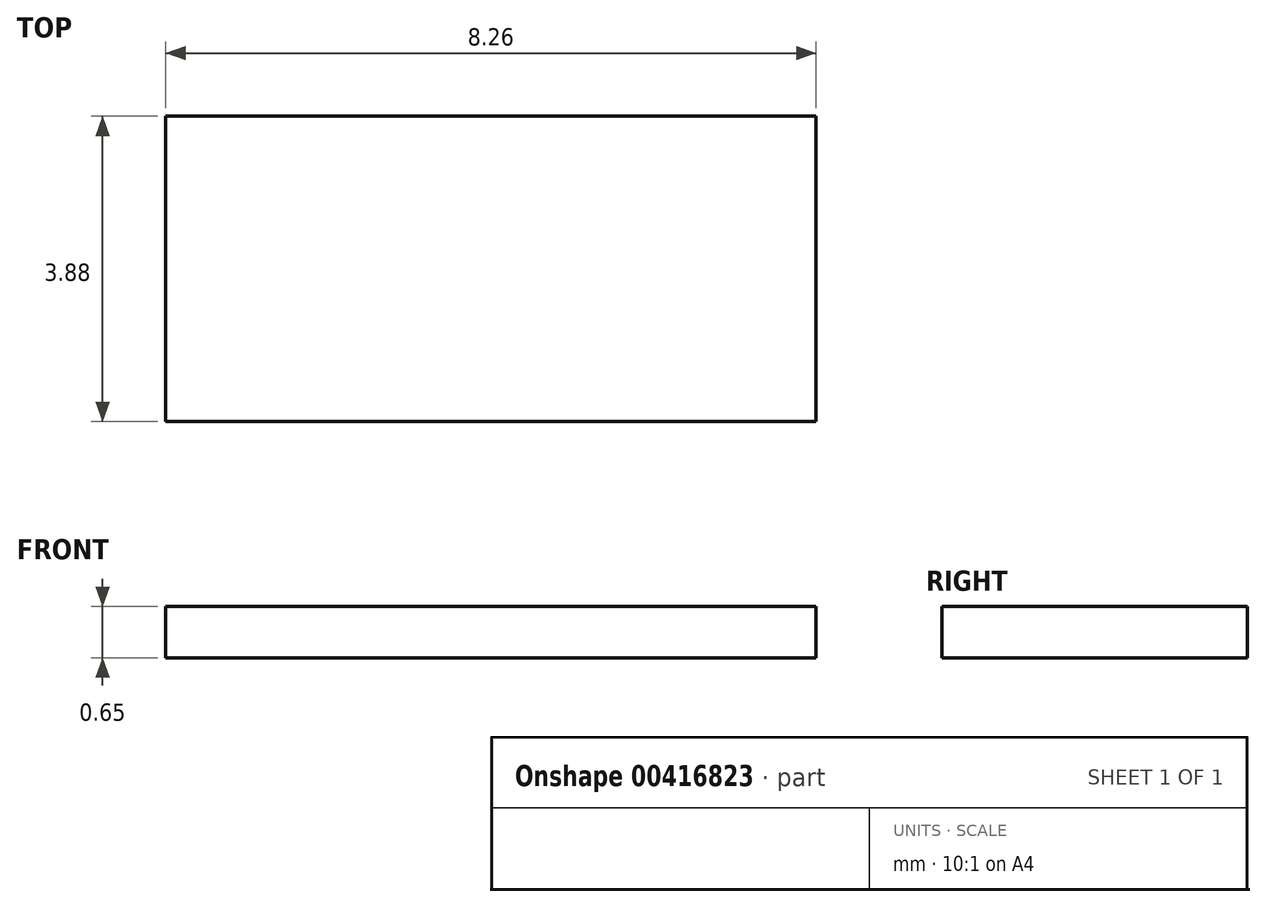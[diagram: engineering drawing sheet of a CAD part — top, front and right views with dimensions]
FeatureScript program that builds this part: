
annotation { "Feature Type Name" : "Feature", "Feature Type Description" : "" }
export const myFeature = defineFeature(function(context is Context, id is Id, definition is map)
    precondition{}
    {
        {
            var Q0;
            Q0=qCreatedBy(makeId("Top.planeOp"),FACE);
            var sketch = newSketch(context, id + "F0", { "sketchPlane" : qUnion([Q0])});
            skLineSegment(sketch, "E0.bottom", {"start": v(0, 0) * mm, "end": v(8.26, 0) * mm});
            skLineSegment(sketch, "E0.top", {"start": v(0, 3.88) * mm, "end": v(8.26, 3.88) * mm});
            skLineSegment(sketch, "E0.left", {"start": v(0, 0) * mm, "end": v(0, 3.88) * mm});
            skLineSegment(sketch, "E0.right", {"start": v(8.26, 0) * mm, "end": v(8.26, 3.88) * mm});
            skSolve(sketch);
        }
        {
            var Q0;
            Q0=makeQuery(id+"F0.imprint","IMPRINT",FACE,{"disambiguationData":[TD([[makeQuery(id+"F0.imprint","IMPRINT",EDGE,{"derivedFrom":sQuery(id+"F0.wireOp",EDGE,"E0.bottom")}),1.0]])]});
            extrude(context, id + "F1", {"entities" : qUnion([Q0]), "depth" : .65 * mm, "offsetDistance" : 25.4 * mm});
        }
    });
